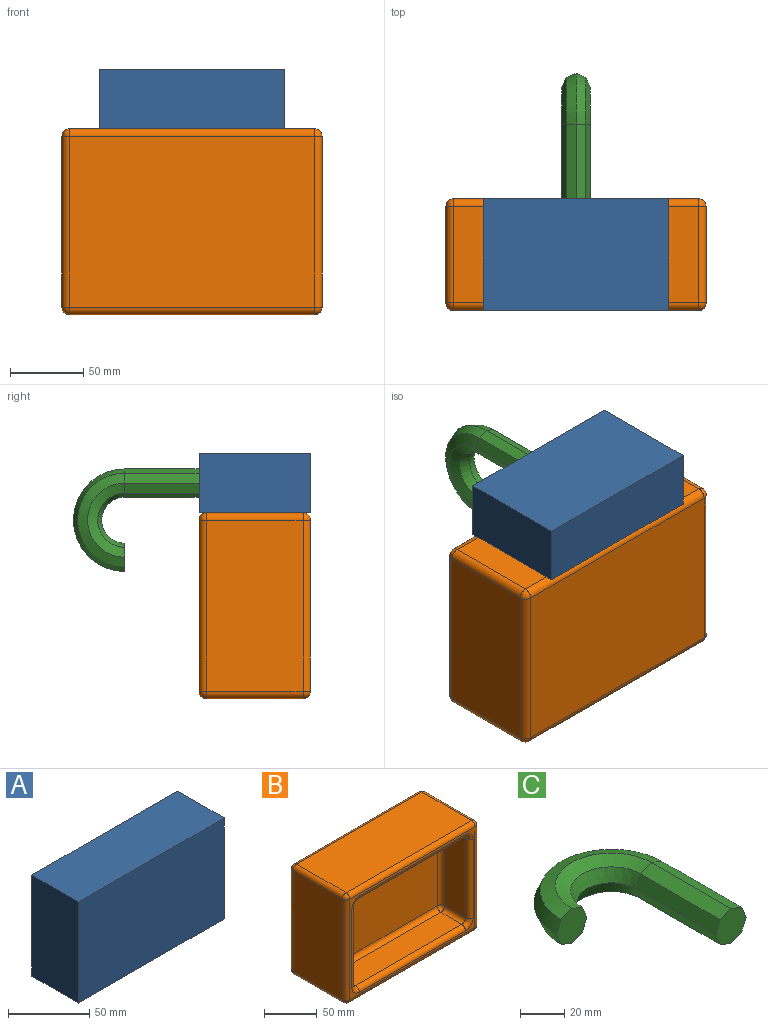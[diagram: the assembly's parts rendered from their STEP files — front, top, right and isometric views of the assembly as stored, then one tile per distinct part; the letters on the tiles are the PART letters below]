
ASSEMBLY  parts=3 mates=2
PART A: 6 faces, bbox 127x40.6x76.2 mm
  f0: plane 127x40.64mm, normal (0,0,1), area 5161.3mm2, adj f1,f3,f4,f5
  f1: plane 76.2x40.64mm, normal (-1,0,0), area 3096.8mm2, adj f0,f2,f4,f5
  f2: plane 127x40.64mm, normal (0,0,-1), area 5161.3mm2, adj f1,f3,f4,f5
  f3: plane 76.2x40.64mm, normal (1,0,0), area 3096.8mm2, adj f0,f2,f4,f5
  f4: plane 127x76.2mm, normal (0,1,0), area 9677.4mm2, adj f0,f1,f2,f3
  f5: plane 127x76.2mm, normal (0,-1,0), area 9677.4mm2, adj f0,f1,f2,f3
PART B: 51 faces, bbox 177.8x76.2x127 mm
  f0: plane 116.84x66.04mm, normal (-1,0,0), area 7716.1mm2, adj f39,f44,f47,f50
  f1: plane 167.64x66.04mm, normal (0,0,-1), area 11070.9mm2, adj f36,f45,f46,f50
  f2: plane 116.84x66.04mm, normal (1,0,0), area 7716.1mm2, adj f31,f35,f36,f37
  f3: plane 142.24x27.94mm, normal (0,0,1), area 3974.2mm2, adj f17,f18,f26,f27
  f4: plane 91.44x27.94mm, normal (1,0,0), area 2554.8mm2, adj f11,f14,f18,f19
  f5: plane 142.24x27.94mm, normal (0,0,-1), area 3974.2mm2, adj f14,f15,f24,f25
  f6: plane 91.44x27.94mm, normal (-1,0,0), area 2554.8mm2, adj f16,f25,f26,f30
  f7: plane 167.64x66.04mm, normal (0,0,1), area 11070.9mm2, adj f31,f34,f38,f39
  f8: plane 167.64x116.84mm, normal (0,-1,0), area 1508mm2, adj f11,f12,f13,f15,f16,f17,f21,f22
  f9: plane 167.64x116.84mm, normal (0,1,0), area 19587.1mm2, adj f37,f38,f46,f47
  f10: plane 142.24x91.44mm, normal (0,-1,0), area 13006.4mm2, adj f19,f24,f27,f30
  f11: cylinder r=5.08mm len=91.44mm, axis (0,0,-1), area 729.7mm2, adj f4,f8,f12,f13
  f12: torus R=10.16mm, axis (0,-1,0), area 86.8mm2, adj f8,f11,f14,f15
  f13: torus R=10.16mm, axis (0,-1,0), area 86.8mm2, adj f8,f11,f17,f18
  f14: cylinder r=5.08mm len=27.94mm, axis (0,1,0), area 223mm2, adj f4,f5,f12,f20
  f15: cylinder r=5.08mm len=142.24mm, axis (-1,0,0), area 1135mm2, adj f5,f8,f12,f21
  f16: cylinder r=5.08mm len=91.44mm, axis (0,0,1), area 729.7mm2, adj f6,f8,f21,f22
  f17: cylinder r=5.08mm len=142.24mm, axis (1,0,0), area 1135mm2, adj f3,f8,f13,f22
  f18: cylinder r=5.08mm len=27.94mm, axis (0,-1,0), area 223mm2, adj f3,f4,f13,f23
  f19: cylinder r=5.08mm len=91.44mm, axis (0,0,1), area 729.7mm2, adj f4,f10,f20,f23
  f20: sphere r=5.08mm, area 40.5mm2, adj f14,f19,f24
  f21: torus R=10.16mm, axis (0,-1,0), area 86.8mm2, adj f8,f15,f16,f25
  f22: torus R=10.16mm, axis (0,-1,0), area 86.8mm2, adj f8,f16,f17,f26
  f23: sphere r=5.08mm, area 40.5mm2, adj f18,f19,f27
  f24: cylinder r=5.08mm len=142.24mm, axis (1,0,0), area 1135mm2, adj f5,f10,f20,f28
  f25: cylinder r=5.08mm len=27.94mm, axis (0,-1,0), area 223mm2, adj f5,f6,f21,f28
  f26: cylinder r=5.08mm len=27.94mm, axis (0,1,0), area 223mm2, adj f3,f6,f22,f29
  f27: cylinder r=5.08mm len=142.24mm, axis (-1,0,0), area 1135mm2, adj f3,f10,f23,f29
  f28: sphere r=5.08mm, area 40.5mm2, adj f24,f25,f30
  f29: sphere r=5.08mm, area 40.5mm2, adj f26,f27,f30
  f30: cylinder r=5.08mm len=91.44mm, axis (0,0,-1), area 729.7mm2, adj f6,f10,f28,f29
  f31: cylinder r=5.08mm len=66.04mm, axis (0,1,0), area 527mm2, adj f2,f7,f32,f33
  f32: sphere r=5.08mm, area 40.5mm2, adj f31,f34,f35
  f33: sphere r=5.08mm, area 40.5mm2, adj f31,f37,f38
  f34: cylinder r=5.08mm len=167.64mm, axis (1,0,0), area 1337.7mm2, adj f7,f8,f32,f40
  f35: cylinder r=5.08mm len=116.84mm, axis (0,0,-1), area 932.3mm2, adj f2,f8,f32,f41
  f36: cylinder r=5.08mm len=66.04mm, axis (0,-1,0), area 527mm2, adj f1,f2,f41,f42
  f37: cylinder r=5.08mm len=116.84mm, axis (0,0,1), area 932.3mm2, adj f2,f9,f33,f42
  f38: cylinder r=5.08mm len=167.64mm, axis (-1,0,0), area 1337.7mm2, adj f7,f9,f33,f43
  f39: cylinder r=5.08mm len=66.04mm, axis (0,-1,0), area 527mm2, adj f0,f7,f40,f43
  f40: sphere r=5.08mm, area 40.5mm2, adj f34,f39,f44
  f41: sphere r=5.08mm, area 40.5mm2, adj f35,f36,f45
  f42: sphere r=5.08mm, area 40.5mm2, adj f36,f37,f46
  f43: sphere r=5.08mm, area 40.5mm2, adj f38,f39,f47
  f44: cylinder r=5.08mm len=116.84mm, axis (0,0,1), area 932.3mm2, adj f0,f8,f40,f48
  f45: cylinder r=5.08mm len=167.64mm, axis (-1,0,0), area 1337.7mm2, adj f1,f8,f41,f48
  f46: cylinder r=5.08mm len=167.64mm, axis (1,0,0), area 1337.7mm2, adj f1,f9,f42,f49
  f47: cylinder r=5.08mm len=116.84mm, axis (0,0,-1), area 932.3mm2, adj f0,f9,f43,f49
  f48: sphere r=5.08mm, area 40.5mm2, adj f44,f45,f50
  f49: sphere r=5.08mm, area 40.5mm2, adj f46,f47,f50
  f50: cylinder r=5.08mm len=66.04mm, axis (0,1,0), area 527mm2, adj f0,f1,f48,f49
PART C: 18 faces, bbox 70x85.8x19.3 mm
  f0: plane 19.31x19.31mm, normal (0,-1,0), area 263.7mm2, adj f2,f3,f4,f5,f6,f7,f8,f9
  f1: plane 19.31x19.31mm, normal (0,-1,0), area 263.7mm2, adj f10,f11,f12,f13,f14,f15,f16,f17
  f2: plane 50.8x6.83mm, normal (0.92,0,0.38), area 375.4mm2, adj f0,f3,f9,f10
  f3: plane 50.8x6.83mm, normal (0.92,0,-0.38), area 375.4mm2, adj f0,f2,f4,f11
  f4: plane 50.8x6.83mm, normal (0.38,0,-0.92), area 375.4mm2, adj f0,f3,f5,f12
  f5: plane 50.8x6.83mm, normal (-0.38,0,-0.92), area 375.4mm2, adj f0,f4,f6,f13
  f6: plane 50.8x6.83mm, normal (-0.92,0,-0.38), area 375.4mm2, adj f0,f5,f7,f14
  f7: plane 50.8x6.83mm, normal (-0.92,0,0.38), area 375.4mm2, adj f0,f6,f8,f15
  f8: plane 50.8x6.83mm, normal (-0.38,0,0.92), area 375.4mm2, adj f0,f7,f9,f16
  f9: plane 50.8x6.83mm, normal (0.38,0,0.92), area 375.4mm2, adj f0,f2,f8,f17
  f10: cone r=32.17mm half-angle=22.5deg, axis (0,0,-1), area 779.7mm2, adj f1,f2,f11,f17
  f11: cone r=34.99mm half-angle=22.5deg, axis (0,0,1), area 779.7mm2, adj f1,f3,f10,f12
  f12: cone r=32.17mm half-angle=67.5deg, axis (0,0,1), area 667.6mm2, adj f1,f4,f11,f13
  f13: cone r=25.34mm half-angle=67.5deg, axis (0,0,-1), area 509mm2, adj f1,f5,f12,f14
  f14: cone r=18.51mm half-angle=22.5deg, axis (0,0,-1), area 396.9mm2, adj f1,f6,f13,f15
  f15: cone r=15.68mm half-angle=22.5deg, axis (0,0,1), area 396.9mm2, adj f1,f7,f14,f16
  f16: cone r=18.51mm half-angle=67.5deg, axis (0,0,1), area 509mm2, adj f1,f8,f15,f17
  f17: cone r=25.34mm half-angle=67.5deg, axis (0,0,-1), area 667.6mm2, adj f1,f9,f10,f16
PLACE A rot(axis=(-1,0,0),90deg) t=(-60.38,-32.45,143.19)mm
PLACE B rot(axis=(1,0,0),180deg) t=(-60.38,-70.55,39.05)mm
PLACE C rot(axis=(0,-1,0),90deg) t=(-60.38,5.65,122.87)mm
MATE fastened C.f0 <-> A.f0  axis (0,-1,0) through (-60.38,5.65,122.87)mm
MATE fastened B.f1 <-> A.f4  axis (0,0,1) through (-60.38,-32.45,102.55)mm
